# Revit family: RN 85120 Optiflex-Profix-Té de raccordement
name_source: partatom
category: Rohrzubehör
units: mm (PartAtom-declared; Revit-internal decimal feet)

## family parameters
Arbeitsebenenbasiert = Nein
Beim Laden mit Abzugskörper schneiden = Nein
Bemaßung runder Anschluss = Durchmesser verwenden
Gemeinsam genutzt = Nein
Immer vertikal = Ja
Teiletyp = T-Stück

## types (2) — shared parameters
1.010.00.2 Blattnummer der Richtlinie = 29
1.010.00.3 Ausgabedatum (Monat) der Richtlinie = 201308
1.010.00.4 Herstellername = R. Nussbaum AG
1.010.00.5 Revisionsdatum der Datei = 20190521
1.010.00.6 Webadresse des Herstellers = http://www.nussbaum.ch
1.100.00.4 Produktbezeichnung = Versorgung
1.110.00.2 Index = 5
1.110.00.4 Produktbezeichnung = Optiflex
1.960/3L.00.8 Link (URL) = https://www.nussbaum.ch
29.700.00.4 Produktname = Optiflex-Profix-Anschluss-T-Stück, mit Wandflansch
29.700.00.5 Produktkennung = 2
29.700.00.6 Querschnittsform = 1
29.700.00.7 Nennweitensystem = DN
29.700.00.8 Nenndrucksystem = PN
29.710.02.4 Nenndruck = 10
29.710.02.5 max. zul. Überdruck [hPa] = 1000
29.710.02.7 max. zul. Dauer-Betriebsdruck [hPa] = 1000
29.710.02.9 max. zul. Dauer-Betriebstemperatur [°C] = 70
CONNECTOR2_DIAMETER_dY_0r = 15 mm
CONNECTOR2_dY_00 = 31 mm
CONNECTOR2_dY_01 = 18 mm
CONNECTOR2_ref_dY = 18 mm
Connector Visibility = Nein
EnclosingSpace Visibility = Nein
Hersteller = R. Nussbaum AG
URL = https://www.nussbaum.ch

## per-type parameters (varying)
| type | 1.800.00.3 TGA-Nummer | 1.800.00.4 Kommentarfeld | 1.810.00.3 Hersteller-Bestellnummer | 1.810.00.4 DATANORM-Nummer | 1.810.00.6 GTIN-Nummer | 29.710.02.10 Formstück-Gewicht [kg] | 29.710.02.3 Benennung | CONNECTOR0_DIAMETER_dX_0r | CONNECTOR0_dX_00 | CONNECTOR0_dX_01 | CONNECTOR0_ref_dX | CONNECTOR1_DIAMETER_dX_0r | CONNECTOR1_dX_00 | CONNECTOR1_dX_01 | CONNECTOR1_ref_dX | Modell | R. Nussbaum AG 85120.21 de Visibility | R. Nussbaum AG 85120.22 de Visibility | Typenkommentare |
| DN=15 | 01900500000000000000000000000000000000000000000091000000000000000002 | 85120.22, Optiflex-Profix-Anschluss-T-Stück, mit Wandflansch, DN=15, L=49, Rp=½ | 85120.22 | 85120.22 | 7612945818478 | 0.221 | Optiflex-Profix-Anschluss-T-Stück, mit Wandflansch, DN=15, L=49, Rp=½ | 15 mm | 20 mm  [stored 0.0656168 ft] | 54 mm | 20 mm  [stored 0.0656168 ft] | 15 mm | 54 mm | 20 mm  [stored 0.0656168 ft] | 20 mm  [stored 0.0656168 ft] | 85120.22 | Nein | Ja | Optiflex-Profix-Té de raccordement  DN=15 |
| DN=12x15x12 | 01900500000000000000000000000000000000000000000091000000000000000001 | 85120.21, Optiflex-Profix-Anschluss-T-Stück, mit Wandflansch, DN=12x15x12, L=49, Rp=½ | 85120.21 | 85120.21 | 7612945818461 | 0.192 | Optiflex-Profix-Anschluss-T-Stück, mit Wandflansch, DN=12x15x12, L=49, Rp=½ | 12 mm  [stored 0.0393701 ft] | 18 mm | 52 mm | 18 mm | 12 mm  [stored 0.0393701 ft] | 52 mm | 18 mm | 18 mm | 85120.21 | Ja | Nein | Optiflex-Profix-Té de raccordement  DN=12x15x12 |

note: [stored X ft] marks values corroborated as IEEE doubles in the binary element streams (Revit-internal decimal feet)

## geometry (parser evidence)
native form markers: Sweep x1
no freeform markers — native parametric forms only
